# Revit family: Roofing-Aquaknight-Scupper_Chamfer-200x75x400x2deg
name_source: partatom
category: Plumbing Fixtures
revit_build: Autodesk Revit 2016 (Build: 20150714_1515(x64)
units: mm (PartAtom-declared; Revit-internal decimal feet)

## family parameters
Always vertical = No
Cut with Voids When Loaded = No
OmniClass Number = 23.60.30.11
OmniClass Title = Pipework Products for General Use
Part Type = Normal
Room Calculation Point = No
Round Connector Dimension = Use Diameter
Shared = No
Work Plane-Based = No

## types (1)
- 200x75x400x2deg
    CW Connection = No
    Connector Y = 40 mm  [stored 0.131234 ft]
    Description = Membrane Scupper 200x75
    HW Connection = No
    Its Large = Yes
    Its Small = No
    Length = 485 mm  [stored 1.59121 ft]
    Manufacturer = Aquanight Industries Ltd
    Material = Aquanight-Black
    Model = 2100.104
    URL = www.aquaknight.co.nz
    Vent Connection = No
    Waste Connection = Yes

note: [stored X ft] marks values corroborated as IEEE doubles in the binary element streams (Revit-internal decimal feet)

## geometry (parser evidence)
native form markers: Sweep x3
no freeform markers — native parametric forms only
